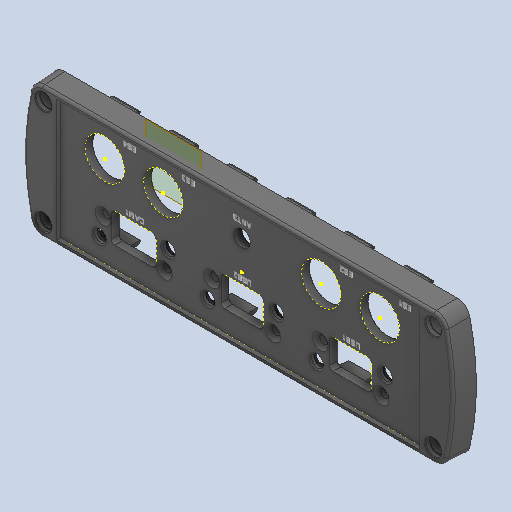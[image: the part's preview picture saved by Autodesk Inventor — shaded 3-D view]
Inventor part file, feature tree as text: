
AUTODESK INVENTOR PART (.ipt)
format: ipt  version: 2024.2 (Build 282272000, 272)  size: 1,064,960 bytes
history: native  units: mm
features: extrude x7, chamfer x5, plane x3, fillet x2, mirror x1, hole x1, sketch x1, other x1
ambient origin geometry x8: Origin, YZ Plane, XZ Plane, XY Plane, X Axis, Y Axis, Z Axis, Center Point
bodies: Solid1 (feature_tree)
feature tree (21):
  extrude  "Extrusion1"  TaperAngle=0.0deg  [1 undecoded]
  fillet  "Fillet1"  Radius=6.9mm
  plane  "Work Plane1"
  extrude  "Extrusion4"  Depth=1.35mm
  chamfer  "Chamfer2"  [1 undecoded]
  mirror  "Mirror1"
  plane  "Work Plane2"
  extrude  "Extrusion7"  Depth=0.2mm
  chamfer  "Chamfer3"  Distance=11.5mm
  hole  "Hole1"  [1 undecoded]
  plane  "Work Plane3"
  extrude  "Extrusion11"  Depth=0.2mm
  extrude  "Extrusion12"  TaperAngle=0.0deg  [1 undecoded]
  fillet  "Fillet4"  Radius=31.0mm
  chamfer  "Chamfer4"  [1 undecoded]
  chamfer  "Chamfer5"  Distance=0.2mm Angle=45.0deg
  extrude  "Extrusion13"  Depth=0.2mm
  sketch  "Sketch20"  dims[d3=9.0mm d15=0.0mm d16=0.0mm d21=6.9mm d23=1.35mm d26=-1.5mm d40=15.4mm d41=11.5mm d42=54.0mm d43=15.4mm d44=0.0mm d45=31.0mm d46=0.0mm d47=0.0mm d48=0.2mm d49=2.0mm d50=45.0deg d65=4.85mm d66=4.85mm d67=27.0mm d68=9.0mm d69=3.3mm d70=3.3mm d71=24.0mm d72=16.55mm d73=11.55mm d74=6.35mm d75=1.85mm d76=5.225mm d77=6.9mm d78=10.075mm d79=10.075mm d80=42.584mm d82=7.0mm d83=10.0mm d84=0.0mm d85=0.5mm d86=2.0mm d87=45.0deg d101=10.075mm d102=4.85mm d103=4.85mm d104=27.0mm d105=9.0mm d106=3.3mm d107=3.3mm d108=24.0mm d109=17.55mm d110=11.55mm d111=6.35mm d112=1.85mm d113=4.725mm d114=10.075mm d115=12.0mm d116=6.9mm d117=42.584mm d118=7.0mm d119=7.0mm d122=12.0mm d127=3.25mm d128=6.0mm d129=6.25mm d130=2.0mm d131=90.0deg d132=8.0mm d133=20.594885mm d136=10.0mm d137=0.0mm d138=0.2mm d139=0.0mm d140=3.0mm d141=0.2mm d142=2.0mm d143=45.0deg d144=0.2mm d145=2.0mm d146=45.0deg d147=10.0mm d148=0.0mm d149=8.0mm d150=12.5mm d151=8.0mm d152=12.5mm d153=12.5mm d154=8.0mm d155=8.0mm d156=12.5mm d157=4.5mm d160=4.5mm d161=1.0mm d164=1.0mm d167=28.699852mm d169=20.0mm d171=42.584mm d172=10.0mm d174=10.0mm d176=7.0mm d177=7.0mm d178=7.0mm d179=1.0mm d180=4.5mm d181=4.725mm d185=6.5mm d186=10.0mm d187=0.0mm d188=0.2mm d189=2.0mm d190=45.0deg]
  extrude  "Extrusion14"  Depth=0.2mm
  chamfer  "Chamfer6"  Distance=10.075mm
  other  "1009799_3D"
note: 5 required parameter values undecoded (feature->parameter linkage not recoverable at this tier; creation-order binding heuristic only, values carry confidence <= 0.55)
